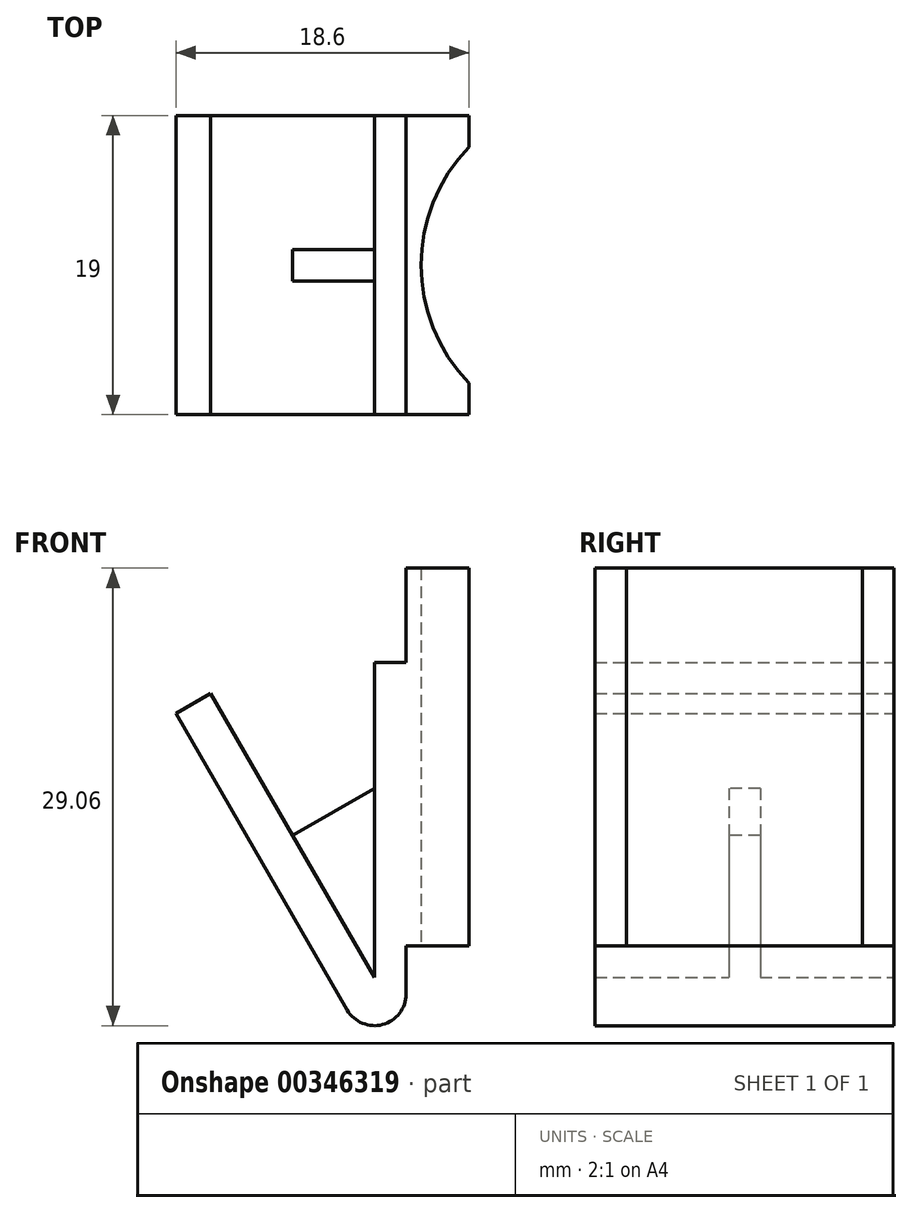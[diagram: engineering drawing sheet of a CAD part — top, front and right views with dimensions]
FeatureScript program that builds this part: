
annotation { "Feature Type Name" : "Feature", "Feature Type Description" : "" }
export const myFeature = defineFeature(function(context is Context, id is Id, definition is map)
    precondition{}
    {
        {
            var Q0;
            Q0=qCreatedBy(makeId("Right.planeOp"),FACE);
            var sketch = newSketch(context, id + "F0", { "sketchPlane" : qUnion([Q0])});
            skLineSegment(sketch, "E0.bottom", {"start": v(9.5, 12) * mm, "end": v(-9.5, 12) * mm});
            skLineSegment(sketch, "E0.top", {"start": v(9.5, -12) * mm, "end": v(-9.5, -12) * mm});
            skLineSegment(sketch, "E0.left", {"start": v(9.5, 12) * mm, "end": v(9.5, -12) * mm});
            skLineSegment(sketch, "E0.right", {"start": v(-9.5, 12) * mm, "end": v(-9.5, -12) * mm});
            skPoint(sketch, "E0.middle", {"position": v(0, 0) * mm});
            skSolve(sketch);
        }
        {
            var Q0;
            Q0 = qSketchRegion(id + "F0", true);
            extrude(context, id + "F1", {"entities" : qUnion([Q0]), "depth" : 4 * mm});
        }
        {
            var Q0;
            Q0=makeQuery(id+"F1.opExtrude","SWEPT_FACE",FACE,{"disambiguationData":[OSD([sQuery(id+"F0.wireOp",EDGE,"E0.left")])]});
            var sketch = newSketch(context, id + "F2", { "sketchPlane" : qUnion([Q0])});
            skPoint(sketch, "E1.orphan", {"position": v(0, 12) * mm});
            skLineSegment(sketch, "E2.bottom", {"start": v(0, 6) * mm, "end": v(2, 6) * mm});
            skLineSegment(sketch, "E2.right", {"start": v(2, 6) * mm, "end": v(2, -14) * mm});
            skLineSegment(sketch, "E3", {"start": v(2, -14) * mm, "end": v(12.41, 4.03) * mm});
            skLineSegment(sketch, "E4", {"start": v(12.41, 4.03) * mm, "end": v(14.6, 2.77) * mm});
            skLineSegment(sketch, "E5", {"start": v(14.6, 2.77) * mm, "end": v(3.73, -16.06) * mm});
            skLineSegment(sketch, "E6", {"start": v(0, 6) * mm, "end": v(0, -15.06) * mm});
            skPoint(sketch, "E7.visualSharp", {"position": v(0, -22.52) * mm});
            skArc(sketch, "E7.filletArc", {"start": v(0, -15.06) * mm, "mid": v(1.48, -17) * mm, "end": v(3.73, -16.06) * mm});
            skSolve(sketch);
        }
        {
            var Q0;
            Q0 = qSketchRegion(id + "F2", true);
            var Q1;
            Q1=makeQuery(id+"F1.opExtrude","CAP_VERTEX",VERTEX,{"disambiguationData":[OSD([sQuery(id+"F0.wireOp",EDGE,"E0.top"),sQuery(id+"F0.wireOp",EDGE,"E0.right")])],"isStart":true});
            extrude(context, id + "F3", {"entities" : qUnion([Q0]), "operationType" : NewBodyOperationType.ADD, "endBound" : BoundingType.UP_TO_VERTEX, "oppositeDirection" : true, "endBoundEntityVertex" : qUnion([Q1]), "depth" : 25 * mm});
        }
        {
            var Q0;
            Q0=makeQuery(id+"F3.opExtrude","SWEPT_FACE",FACE,{"disambiguationData":[OSD([sQuery(id+"F2.wireOp",EDGE,"E3")])]});
            var sketch = newSketch(context, id + "F4", { "sketchPlane" : qUnion([Q0])});
            skLineSegment(sketch, "E8", {"start": v(0, 9.7) * mm, "end": v(0, -11.12) * mm, "construction": true});
            skPoint(sketch, "E9.middle", {"position": v(0, 0) * mm});
            skLineSegment(sketch, "E10.top", {"start": v(1, -11.12) * mm, "end": v(-1, -11.12) * mm});
            skLineSegment(sketch, "E10.left", {"start": v(1, -0.71) * mm, "end": v(1, -11.12) * mm});
            skLineSegment(sketch, "E10.right", {"start": v(-1, -0.71) * mm, "end": v(-1, -11.12) * mm});
            skPoint(sketch, "E10.middle", {"position": v(0, -0.71) * mm});
            skLineSegment(sketch, "E11", {"start": v(1, -0.71) * mm, "end": v(-1, -0.71) * mm});
            skPoint(sketch, "E12.orphan", {"position": v(1, 9.7) * mm});
            skPoint(sketch, "E13.orphan", {"position": v(-1, 9.7) * mm});
            skSolve(sketch);
        }
        {
            var Q0;
            Q0 = qSketchRegion(id + "F4", true);
            var Q1;
            Q1=makeQuery(id+"F3.opExtrude","SWEPT_FACE",FACE,{"disambiguationData":[OSD([sQuery(id+"F2.wireOp",EDGE,"E2.right")])]});
            extrude(context, id + "F5", {"entities" : qUnion([Q0]), "operationType" : NewBodyOperationType.ADD, "endBound" : BoundingType.UP_TO_SURFACE, "endBoundEntityFace" : qUnion([Q1]), "depth" : 25 * mm});
        }
        {
            var Q0;
            Q0=makeQuery(id+"F1.opExtrude","SWEPT_FACE",FACE,{"disambiguationData":[OSD([sQuery(id+"F0.wireOp",EDGE,"E0.top")])]});
            var sketch = newSketch(context, id + "F6", { "sketchPlane" : qUnion([Q0])});
            skPoint(sketch, "E14.centerSnap0", {"position": v(4, 0) * mm});
            skArc(sketch, "E15", {"start": v(4, 7.5) * mm, "mid": v(0.97, 0) * mm, "end": v(4, -7.5) * mm});
            skLineSegment(sketch, "E16", {"start": v(0, 0) * mm, "end": v(11.75, 0) * mm, "construction": true});
            skLineSegment(sketch, "E17", {"start": v(4, 7.5) * mm, "end": v(4, -7.5) * mm});
            skSolve(sketch);
        }
        {
            var Q0;
            Q0 = qSketchRegion(id + "F6", true);
            extrude(context, id + "F7", {"entities" : qUnion([Q0]), "operationType" : NewBodyOperationType.REMOVE, "endBound" : BoundingType.THROUGH_ALL, "oppositeDirection" : true, "depth" : 25 * mm});
        }
    });
